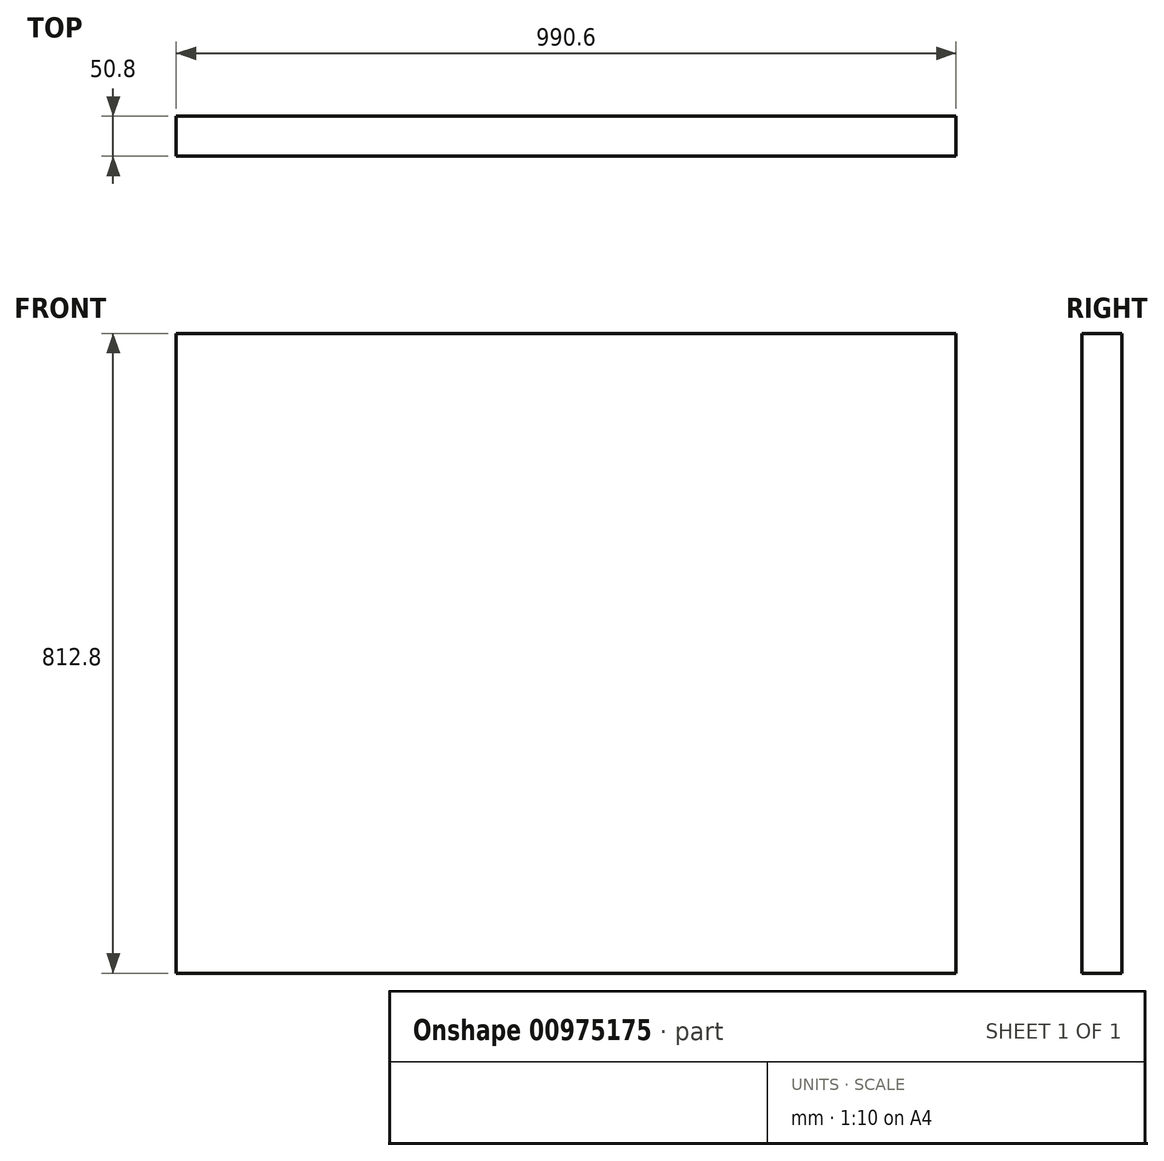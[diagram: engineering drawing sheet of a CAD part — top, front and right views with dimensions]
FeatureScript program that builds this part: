
annotation { "Feature Type Name" : "Feature", "Feature Type Description" : "" }
export const myFeature = defineFeature(function(context is Context, id is Id, definition is map)
    precondition{}
    {
        {
            var Q0;
            Q0=qCreatedBy(makeId("Top.planeOp"),FACE);
            var sketch = newSketch(context, id + "F0", { "sketchPlane" : qUnion([Q0])});
            skLineSegment(sketch, "E0.bottom", {"start": v(-1068.33, 18.94) * mm, "end": v(-52.33, 18.94) * mm});
            skLineSegment(sketch, "E0.top", {"start": v(-1068.33, -31.86) * mm, "end": v(-52.33, -31.86) * mm});
            skLineSegment(sketch, "E0.left", {"start": v(-1068.33, 18.94) * mm, "end": v(-1068.33, -31.86) * mm});
            skLineSegment(sketch, "E0.right", {"start": v(-52.33, 18.94) * mm, "end": v(-52.33, -31.86) * mm});
            skSolve(sketch);
        }
        {
            var Q0;
            Q0=makeQuery(id+"F0.imprint","IMPRINT",FACE,{"disambiguationData":[TD([[makeQuery(id+"F0.imprint","IMPRINT",EDGE,{"derivedFrom":sQuery(id+"F0.wireOp",EDGE,"E0.bottom")}),-1.0]])]});
            extrude(context, id + "F1", {"entities" : qUnion([Q0]), "depth" : 812.8 * mm, "offsetDistance" : 25.4 * mm});
        }
        {
            var Q0;
            Q0=makeQuery(id+"F1.opExtrude","SWEPT_FACE",FACE,{"disambiguationData":[OSD([sQuery(id+"F0.wireOp",EDGE,"E0.right")])]});
            extrude(context, id + "F2", {"entities" : qUnion([Q0]), "operationType" : NewBodyOperationType.REMOVE, "oppositeDirection" : true, "depth" : 12.7 * mm, "offsetDistance" : 25.4 * mm});
        }
        {
            var Q0;
            Q0=makeQuery(id+"F2.boolean.opBoolean","COPY",FACE,{"derivedFrom":makeQuery(id+"F2.opExtrude","CAP_FACE",FACE,{"disambiguationData":[OSD([sQuery(id+"F0.wireOp",EDGE,"E0.right")])],"isStart":false})});
            extrude(context, id + "F3", {"entities" : qUnion([Q0]), "operationType" : NewBodyOperationType.REMOVE, "oppositeDirection" : true, "depth" : 12.7 * mm, "offsetDistance" : 25.4 * mm});
        }
    });
